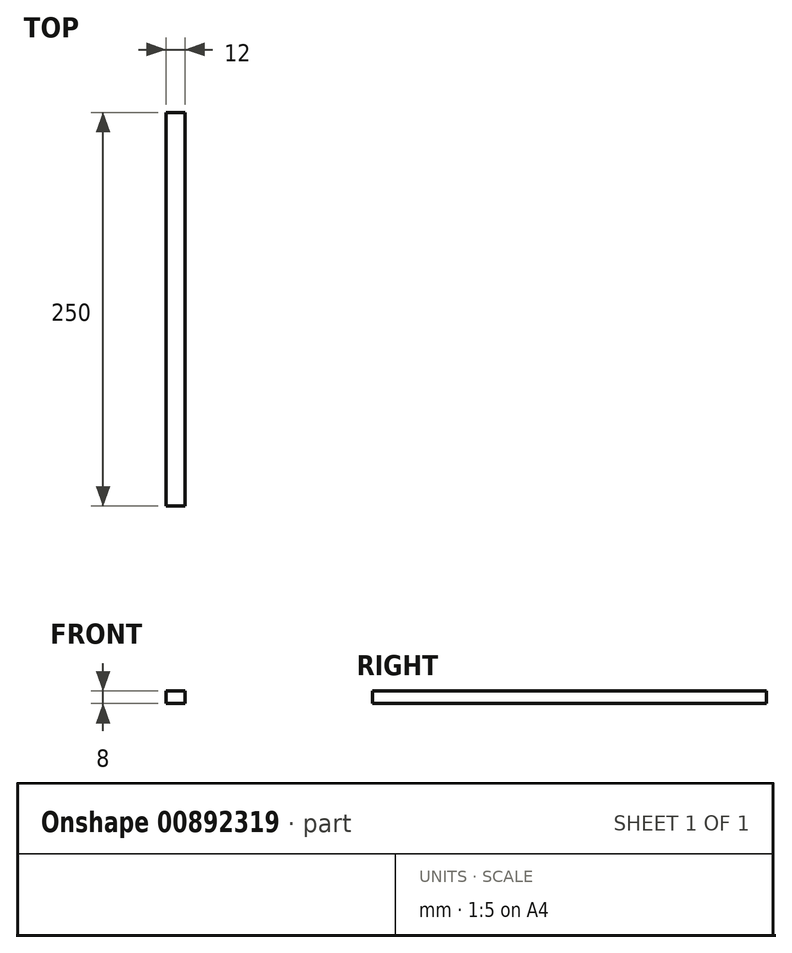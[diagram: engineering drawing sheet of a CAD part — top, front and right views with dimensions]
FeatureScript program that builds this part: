
annotation { "Feature Type Name" : "Feature", "Feature Type Description" : "" }
export const myFeature = defineFeature(function(context is Context, id is Id, definition is map)
    precondition{}
    {
        {
            var Q0;
            Q0=qCreatedBy(makeId("Front.planeOp"),FACE);
            var sketch = newSketch(context, id + "F0", { "sketchPlane" : qUnion([Q0])});
            skLineSegment(sketch, "E0.bottom", {"start": v(6, -4) * mm, "end": v(-6, -4) * mm});
            skLineSegment(sketch, "E0.top", {"start": v(6, 4) * mm, "end": v(-6, 4) * mm});
            skLineSegment(sketch, "E0.left", {"start": v(6, -4) * mm, "end": v(6, 4) * mm});
            skLineSegment(sketch, "E0.right", {"start": v(-6, -4) * mm, "end": v(-6, 4) * mm});
            skPoint(sketch, "E0.middle", {"position": v(0, 0) * mm});
            skSolve(sketch);
        }
        {
            var Q0;
            Q0=makeQuery(id+"F0.imprint","IMPRINT",FACE,{"disambiguationData":[TD([[makeQuery(id+"F0.imprint","IMPRINT",EDGE,{"derivedFrom":sQuery(id+"F0.wireOp",EDGE,"E0.bottom")}),-1.0]])]});
            extrude(context, id + "F1", {"entities" : qUnion([Q0]), "oppositeDirection" : true, "depth" : 250 * mm, "offsetDistance" : 25 * mm});
        }
    });
